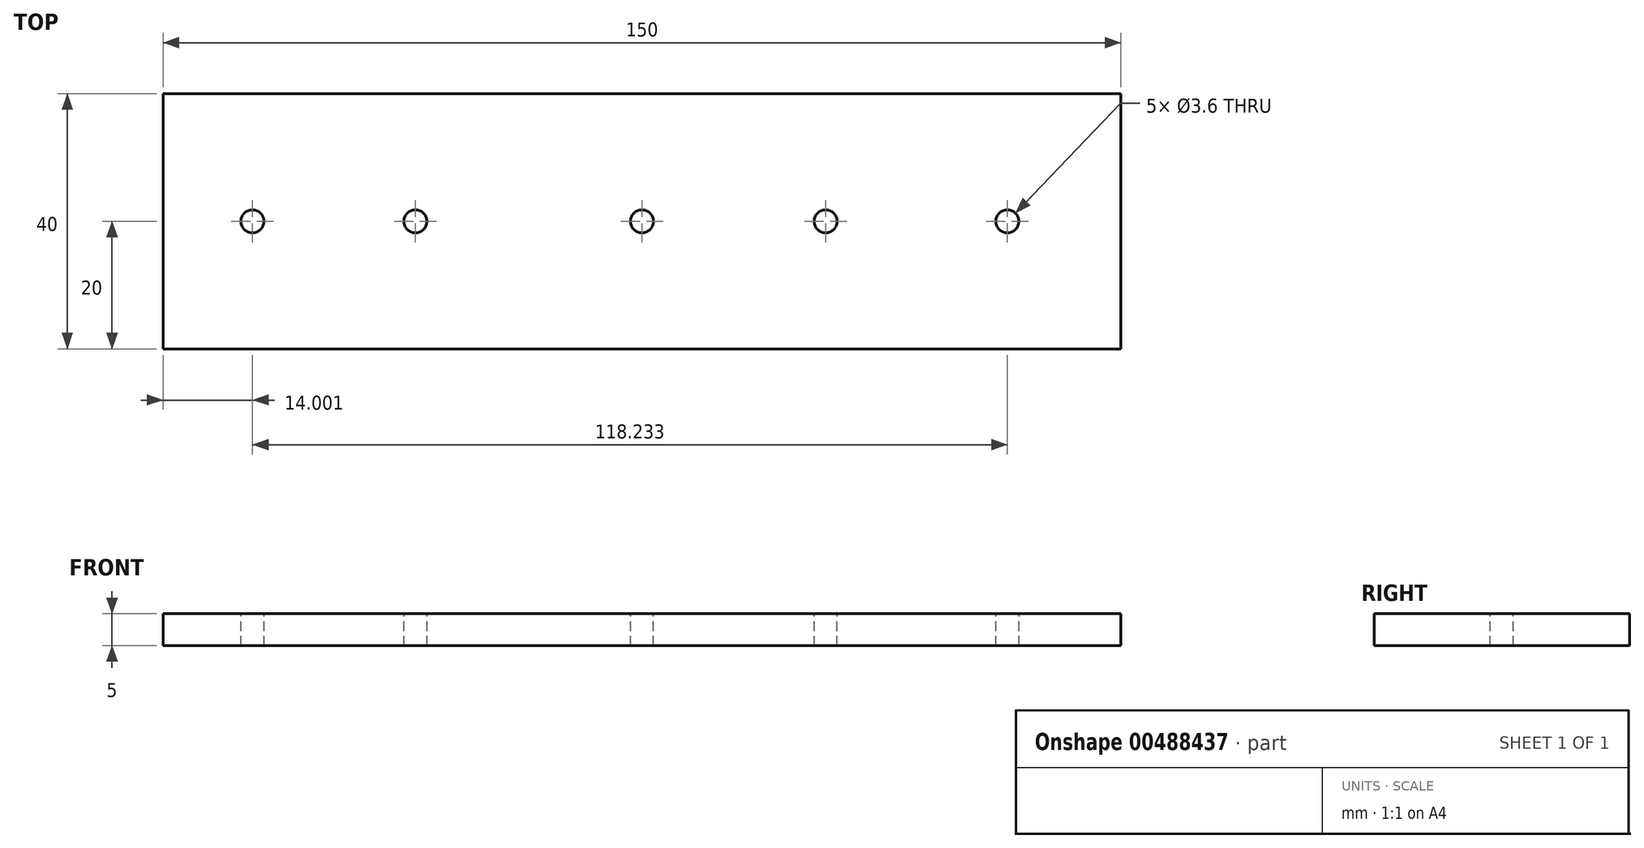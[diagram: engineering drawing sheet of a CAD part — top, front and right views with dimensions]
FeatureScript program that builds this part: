
annotation { "Feature Type Name" : "Feature", "Feature Type Description" : "" }
export const myFeature = defineFeature(function(context is Context, id is Id, definition is map)
    precondition{}
    {
        {
            var Q0;
            Q0=qCreatedBy(makeId("Top.planeOp"),FACE);
            var sketch = newSketch(context, id + "F0", { "sketchPlane" : qUnion([Q0])});
            skLineSegment(sketch, "E0.bottom", {"start": v(75, 20) * mm, "end": v(-75, 20) * mm});
            skLineSegment(sketch, "E0.top", {"start": v(75, -20) * mm, "end": v(-75, -20) * mm});
            skLineSegment(sketch, "E0.left", {"start": v(75, 20) * mm, "end": v(75, -20) * mm});
            skLineSegment(sketch, "E0.right", {"start": v(-75, 20) * mm, "end": v(-75, -20) * mm});
            skPoint(sketch, "E0.middle", {"position": v(0, 0) * mm});
            skSolve(sketch);
        }
        {
            var Q0;
            Q0 = qSketchRegion(id + "F0", true);
            extrude(context, id + "F1", {"entities" : qUnion([Q0]), "endBound" : BoundingType.SYMMETRIC, "oppositeDirection" : true, "depth" : 5 * mm});
        }
        {
            var Q0;
            Q0=makeQuery(id+"F1.opExtrude","CAP_FACE",FACE,{"disambiguationData":[OSD([sQuery(id+"F0.wireOp",EDGE,"E0.bottom"),sQuery(id+"F0.wireOp",EDGE,"E0.top"),sQuery(id+"F0.wireOp",EDGE,"E0.left"),sQuery(id+"F0.wireOp",EDGE,"E0.right")])],"isStart":true});
            var sketch = newSketch(context, id + "F2", { "sketchPlane" : qUnion([Q0])});
            skCircle(sketch, "E1", {"center": v(57.23, 0) * mm, "radius": 1.8 * mm});
            skCircle(sketch, "E2", {"center": v(28.76, 0) * mm, "radius": 1.8 * mm});
            skCircle(sketch, "E3", {"center": v(0, 0) * mm, "radius": 1.8 * mm});
            skCircle(sketch, "E4", {"center": v(-35.48, 0) * mm, "radius": 1.8 * mm});
            skCircle(sketch, "E5", {"center": v(-61, 0) * mm, "radius": 1.8 * mm});
            skSolve(sketch);
        }
        {
            var Q0;
            Q0 = qSketchRegion(id + "F2", true);
            extrude(context, id + "F3", {"entities" : qUnion([Q0]), "operationType" : NewBodyOperationType.REMOVE, "oppositeDirection" : true, "depth" : 8 * mm});
        }
    });
